# Revit family: IS_Connect2_K9293_BIM_IT
name_source: partatom
category: Plumbing Fixtures
revit_build: Autodesk Revit 2017 (Build: 20160225_1515(x64)
units: mm (PartAtom-declared; Revit-internal decimal feet)

## family parameters
Always vertical = No
Cut with Voids When Loaded = No
OmniClass Number = 23.45.05.14.21.11
OmniClass Title = Bath/Shower Units
Part Type = Normal
Room Calculation Point = No
Round Connector Dimension = Use Diameter
Shared = No
Work Plane-Based = No

## types (1)
- K9293EO - EU 850 SALOON
    Accessori = http://www.idealstandard.it
    AltezzaNominale = 0 mm  [stored 0 ft]
    Autore = Ideal Standard
    Caratteristiche = Connect2 850 SALOON
    CodiceABarre = 8014140456315
    Colore = Vetro Transparente
    CostoDiSostituzione = 0 $
    Description = Porta doccia tipo saloon con ante battenti con vetro temperato 6 mm, trattamento Ideal Clean, maniglia cromata, sistema Click&Clean e reversibile
    DescrizioneClassifcazioneUni2015 = Shower enclosures
    Desrizione = Porta doccia tipo saloon con ante battenti con vetro temperato 6 mm, trattamento Ideal Clean, maniglia cromata, sistema Click&Clean e reversibile
    Dimensione = 1950 x 0 x 29mm
    DimensioneScarico = 0
    DurataGaranzia = 2
    DurataGaranziaProdotti = 2
    Finitura = Vetro Trasparente
    Forma = Regtangolare
    Garanzia = Garanzia Idealstandard
    IfcEsportaCome = IfcFurnitureType
    InformaziniGaranzia = www.idealstandard.it/garanzia.html
    InformazioniDiProdotto = http://www.idealstandard.it
    InformazioniGaranzia = www.idealstandard.it/garanzia.html
    Installation instructions = https://www.idealspec.co.uk
    InstruzioniInstallazione = www.idealstandard.it/prodotti/html
    LarghezzaNominale = 0 mm  [stored 0 ft]
    LunghezzaNominale = 850 mm  [stored 2.78871 ft]
    Maniglia = No
    Manufacturer = www.idealstandard.it
    Materiale = Vetro Temperato
    Model = K9293EO
    ModelloDiRiferimento = K9293
    Nome = ShowerEnclosure_CONNECT-2-K9382EO_IdealStandard
    NomeOggettoBim = ISI_IdealStandard_ShowersEnclosures_Connect2_K9382EO
    Nominal depth = 0
    Nominal height = 1950
    NumeroDiModello = K9382EO
    PartiDiRicambio = www.idealstandard.it
    PesoNetto = 29
    PiattoDoccia = No
    Product group = Shower Enclosure
    Produttore = Ideal Standard
    ProfonditaNominale = 0 mm  [stored 0 ft]
    Riferimento = CONNECT 2 SALOON DOOR 85 CLEAR GLASS BRIGHT SILVER FINISH
    RiferimentoClassificazioneUni2015 = Pr_40_20_06_79
    SeatMaterial = 0 mm  [stored 0 ft]
    Spazio = Interno
    SpessoreDelMateriale = 0
    SpilloverLivello = 0
    Telefono = 800 652 290
    TipoEspotazioneIfc = USERDEFINED
    Uniclass 2015 Code = Pr_40_20_06_79
    Uniclass 2015 Name = Shower enclosures
    UnitàDurata = Anno
    UnitàDurataGaranzia = Anno
    UnitàLineare = millimitri
    UnitàMonetaria = €
    UnitàSuperficie = millimitri
    UnitàVolume = Litri
    Versione = 1
    VersioneClassificazioneUni2015 = v1.15
    Weight Net (Kg) = 29

note: [stored X ft] marks values corroborated as IEEE doubles in the binary element streams (Revit-internal decimal feet)

## geometry (parser evidence)
native form markers: Sweep x4
no freeform markers — native parametric forms only
